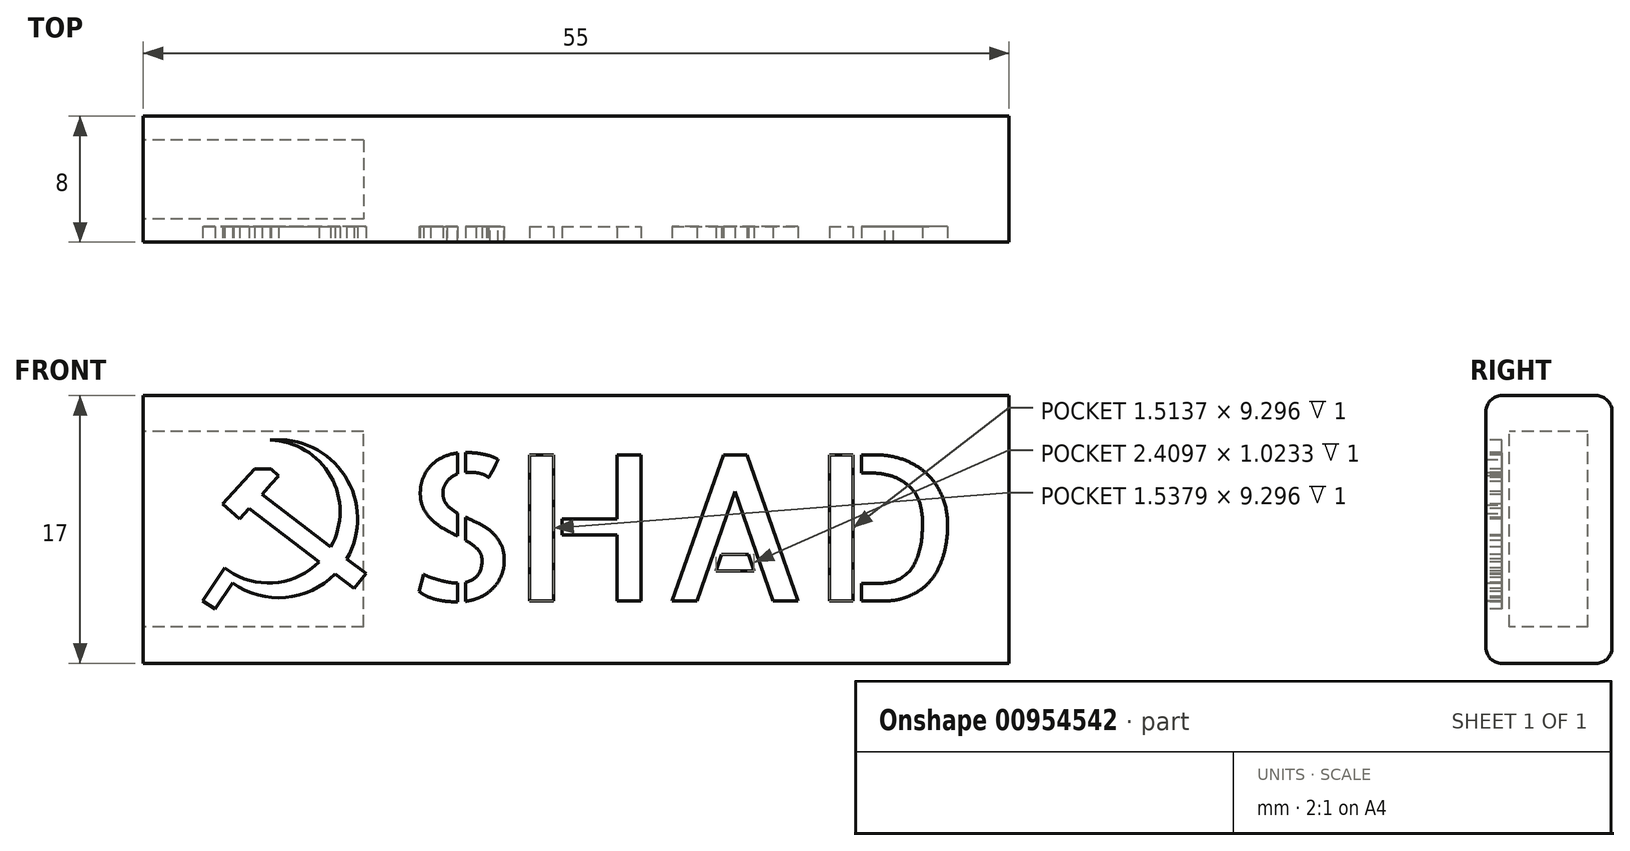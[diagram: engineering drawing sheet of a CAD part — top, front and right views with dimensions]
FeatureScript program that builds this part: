
annotation { "Feature Type Name" : "Feature", "Feature Type Description" : "" }
export const myFeature = defineFeature(function(context is Context, id is Id, definition is map)
    precondition{}
    {
        {
            var Q0;
            Q0=qCreatedBy(makeId("Top.planeOp"),FACE);
            var sketch = newSketch(context, id + "F0", { "sketchPlane" : qUnion([Q0])});
            skLineSegment(sketch, "E0.bottom", {"start": v(-6.9, 4.32) * mm, "end": v(8.1, 4.32) * mm});
            skLineSegment(sketch, "E0.top", {"start": v(-6.9, -3.68) * mm, "end": v(8.1, -3.68) * mm});
            skLineSegment(sketch, "E0.left", {"start": v(-7.9, 3.32) * mm, "end": v(-7.9, -2.68) * mm});
            skLineSegment(sketch, "E0.right", {"start": v(9.1, 3.32) * mm, "end": v(9.1, -2.68) * mm});
            skPoint(sketch, "E0.middle", {"position": v(0.6, 0.32) * mm});
            skPoint(sketch, "E1.visualSharp", {"position": v(-7.9, 4.32) * mm});
            skArc(sketch, "E1.filletArc", {"start": v(-6.9, 4.32) * mm, "mid": v(-7.6, 4.03) * mm, "end": v(-7.9, 3.32) * mm});
            skPoint(sketch, "E2.visualSharp", {"position": v(9.1, 4.32) * mm});
            skArc(sketch, "E2.filletArc", {"start": v(9.1, 3.32) * mm, "mid": v(8.81, 4.03) * mm, "end": v(8.1, 4.32) * mm});
            skPoint(sketch, "E3.visualSharp", {"position": v(-7.9, -3.68) * mm});
            skArc(sketch, "E3.filletArc", {"start": v(-7.9, -2.68) * mm, "mid": v(-7.6, -3.38) * mm, "end": v(-6.9, -3.68) * mm});
            skPoint(sketch, "E4.visualSharp", {"position": v(9.1, -3.68) * mm});
            skArc(sketch, "E4.filletArc", {"start": v(8.1, -3.68) * mm, "mid": v(8.81, -3.38) * mm, "end": v(9.1, -2.68) * mm});
            skSolve(sketch);
        }
        {
            var Q0;
            Q0 = qSketchRegion(id + "F0", true);
            extrude(context, id + "F1", {"entities" : qUnion([Q0]), "depth" : 55 * mm, "offsetDistance" : 25 * mm});
        }
        {
            var Q0;
            Q0=makeQuery(id+"F1.opExtrude","CAP_FACE",FACE,{"disambiguationData":[OSD([sQuery(id+"F0.wireOp",EDGE,"E0.bottom"),sQuery(id+"F0.wireOp",EDGE,"E0.top"),sQuery(id+"F0.wireOp",EDGE,"E0.left"),sQuery(id+"F0.wireOp",EDGE,"E0.right"),sQuery(id+"F0.wireOp",EDGE,"E1.filletArc"),sQuery(id+"F0.wireOp",EDGE,"E2.filletArc"),sQuery(id+"F0.wireOp",EDGE,"E3.filletArc"),sQuery(id+"F0.wireOp",EDGE,"E4.filletArc")])],"isStart":false});
            var sketch = newSketch(context, id + "F2", { "sketchPlane" : qUnion([Q0])});
            skPoint(sketch, "E5.middle", {"position": v(-0.27, 0.65) * mm});
            skLineSegment(sketch, "E6.bottom", {"start": v(-5.58, 2.8) * mm, "end": v(6.82, 2.8) * mm});
            skLineSegment(sketch, "E6.top", {"start": v(-5.58, -2.2) * mm, "end": v(6.82, -2.2) * mm});
            skLineSegment(sketch, "E6.left", {"start": v(-5.58, 2.8) * mm, "end": v(-5.58, -2.2) * mm});
            skLineSegment(sketch, "E6.right", {"start": v(6.82, 2.8) * mm, "end": v(6.82, -2.2) * mm});
            skPoint(sketch, "E6.middle", {"position": v(0.62, 0.3) * mm});
            skSolve(sketch);
        }
        {
            var Q0;
            Q0 = qSketchRegion(id + "F2", true);
            extrude(context, id + "F3", {"entities" : qUnion([Q0]), "operationType" : NewBodyOperationType.REMOVE, "oppositeDirection" : true, "depth" : 14 * mm, "offsetDistance" : 25 * mm});
        }
        {
            var Q0;
            Q0=makeQuery(id+"F1.opExtrude","SWEPT_BODY",BODY,{"disambiguationData":[OSD([sQuery(id+"F0.wireOp",EDGE,"E0.bottom"),sQuery(id+"F0.wireOp",EDGE,"E0.top"),sQuery(id+"F0.wireOp",EDGE,"E0.left"),sQuery(id+"F0.wireOp",EDGE,"E0.right"),sQuery(id+"F0.wireOp",EDGE,"E1.filletArc"),sQuery(id+"F0.wireOp",EDGE,"E2.filletArc"),sQuery(id+"F0.wireOp",EDGE,"E3.filletArc"),sQuery(id+"F0.wireOp",EDGE,"E4.filletArc")])]});
            var Q1;
            Q1=sQuery(id+"F0.wireOp",EDGE,"E0.right");
            transform(context, id + "F4", {"entities" : qUnion([Q0]), "transformType" : TransformType.ROTATION, "transformAxis" : qUnion([Q1]), "angle" : 90 * degree, "makeCopy" : false});
        }
        {
            var Q0;
            Q0=makeQuery(id+"F1.opExtrude","SWEPT_FACE",FACE,{"disambiguationData":[OSD([sQuery(id+"F0.wireOp",EDGE,"E0.top")])]});
            var sketch = newSketch(context, id + "F5", { "sketchPlane" : qUnion([Q0])});
            skText(sketch, "E7", { "text": "SHAD", "fontName": "AllertaStencil-Regular.ttf"});
            skLineSegment(sketch, "E8", {"start": v(-40.84, -6.87) * mm, "end": v(-38.82, -4.65) * mm});
            skLineSegment(sketch, "E9", {"start": v(-38.82, -4.65) * mm, "end": v(-37.76, -5.62) * mm});
            skLineSegment(sketch, "E10", {"start": v(-37.76, -5.62) * mm, "end": v(-39.78, -7.84) * mm});
            skLineSegment(sketch, "E11", {"start": v(-39.78, -7.84) * mm, "end": v(-40.84, -6.87) * mm});
            skLineSegment(sketch, "E12", {"start": v(-38.82, -4.65) * mm, "end": v(-37.76, -4.65) * mm});
            skLineSegment(sketch, "E13", {"start": v(-37.76, -4.65) * mm, "end": v(-37.28, -5.09) * mm});
            skLineSegment(sketch, "E14", {"start": v(-37.28, -5.09) * mm, "end": v(-37.76, -5.62) * mm});
            skLineSegment(sketch, "E15", {"start": v(-42.1, -13.03) * mm, "end": v(-40.72, -10.94) * mm});
            skLineSegment(sketch, "E16", {"start": v(-40.72, -10.94) * mm, "end": v(-39.93, -11.47) * mm});
            skLineSegment(sketch, "E17", {"start": v(-39.93, -11.47) * mm, "end": v(-41.31, -13.55) * mm});
            skLineSegment(sketch, "E18", {"start": v(-41.31, -13.55) * mm, "end": v(-42.1, -13.03) * mm});
            skArc(sketch, "E19", {"start": v(-40.72, -10.94) * mm, "mid": v(-33.65, -8.89) * mm, "end": v(-37.83, -2.83) * mm});
            skArc(sketch, "E20", {"start": v(-40.21, -11.9) * mm, "mid": v(-32.44, -9.1) * mm, "end": v(-37.83, -2.83) * mm});
            skLineSegment(sketch, "E21", {"start": v(-38.35, -6.27) * mm, "end": v(-31.75, -11.3) * mm});
            skLineSegment(sketch, "E22", {"start": v(-31.75, -11.3) * mm, "end": v(-32.48, -12.26) * mm});
            skLineSegment(sketch, "E23", {"start": v(-32.48, -12.26) * mm, "end": v(-39.17, -7.17) * mm});
            skLineSegment(sketch, "E24", {"start": v(-39.17, -7.17) * mm, "end": v(-38.35, -6.27) * mm});
            const initialGuessF5  = {"E7": [-0.02938, -0.01305, 1, 0, 0.0093]};
            skSetInitialGuess(sketch, initialGuessF5);
            skSolve(sketch);
        }
        {
            var Q0;
            Q0 = qSketchRegion(id + "F5", true);
            var Q1;
            Q1=makeQuery(id+"F5.imprint","IMPRINT",FACE,{"disambiguationData":[TD([[makeQuery(id+"F5.imprint","IMPRINT",EDGE,{"derivedFrom":sQuery(id+"F5.wireOp",EDGE,"E7.sketch_text.stroke-50")}),-1.0]])]});
            var Q2;
            Q2=makeQuery(id+"F5.imprint","IMPRINT",FACE,{"disambiguationData":[TD([[makeQuery(id+"F5.imprint","IMPRINT",EDGE,{"derivedFrom":sQuery(id+"F5.wireOp",EDGE,"E7.sketch_text.stroke-73")}),-1.0]])]});
            var Q3;
            Q3=makeQuery(id+"F5.imprint","IMPRINT",FACE,{"disambiguationData":[TD([[makeQuery(id+"F5.imprint","IMPRINT",EDGE,{"derivedFrom":sQuery(id+"F5.wireOp",EDGE,"E7.sketch_text.stroke-25")}),-1.0]])]});
            var Q4;
            Q4=makeQuery(id+"F5.imprint","IMPRINT",FACE,{"disambiguationData":[TD([[makeQuery(id+"F5.imprint","IMPRINT",EDGE,{"derivedFrom":sQuery(id+"F5.wireOp",EDGE,"E7.sketch_text.stroke-62")}),-1.0]])]});
            var Q5;
            Q5=makeQuery(id+"F5.imprint","IMPRINT",FACE,{"disambiguationData":[TD([[makeQuery(id+"F5.imprint","IMPRINT",EDGE,{"derivedFrom":sQuery(id+"F5.wireOp",EDGE,"E7.sketch_text.stroke-0")}),-1.0]])]});
            var Q6;
            Q6=makeQuery(id+"F5.imprint","IMPRINT",FACE,{"disambiguationData":[TD([[makeQuery(id+"F5.imprint","IMPRINT",EDGE,{"derivedFrom":sQuery(id+"F5.wireOp",EDGE,"E7.sketch_text.stroke-58")}),-1.0]])]});
            var Q7;
            Q7=makeQuery(id+"F5.imprint","IMPRINT",FACE,{"disambiguationData":[TD([[makeQuery(id+"F5.imprint","IMPRINT",EDGE,{"derivedFrom":sQuery(id+"F5.wireOp",EDGE,"E7.sketch_text.stroke-11")}),-1.0]])]});
            var Q8;
            Q8=makeQuery(id+"F5.imprint","IMPRINT",FACE,{"disambiguationData":[TD([[makeQuery(id+"F5.imprint","IMPRINT",EDGE,{"derivedFrom":sQuery(id+"F5.wireOp",EDGE,"E7.sketch_text.stroke-69")}),-1.0]])]});
            var Q9;
            Q9=makeQuery(id+"F5.imprint","IMPRINT",FACE,{"disambiguationData":[TD([[makeQuery(id+"F5.imprint","IMPRINT",EDGE,{"derivedFrom":sQuery(id+"F5.wireOp",EDGE,"E7.sketch_text.stroke-37")}),-1.0]])]});
            var Q10;
            Q10=makeQuery(id+"F5.imprint","IMPRINT",FACE,{"disambiguationData":[TD([[makeQuery(id+"F5.imprint","IMPRINT",EDGE,{"derivedFrom":sQuery(id+"F5.wireOp",EDGE,"E7.sketch_text.stroke-77")}),-1.0]])]});
            extrude(context, id + "F6", {"entities" : qUnion([Q0, Q1, Q2, Q3, Q4, Q5, Q6, Q7, Q8, Q9, Q10]), "operationType" : NewBodyOperationType.REMOVE, "oppositeDirection" : true, "depth" : 1 * mm, "offsetDistance" : 25 * mm});
        }
    });
